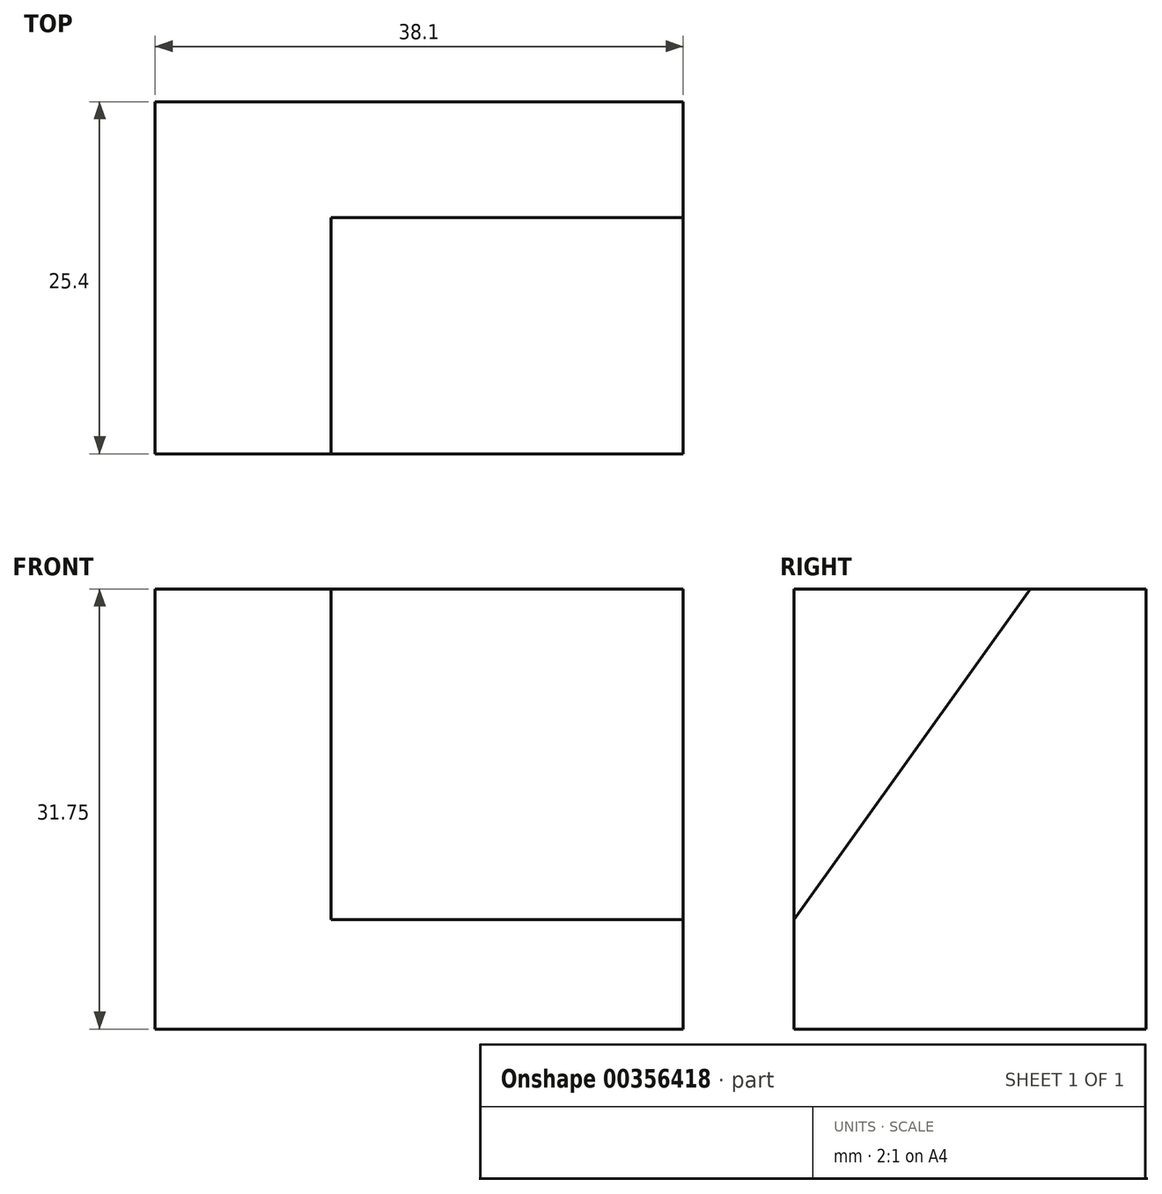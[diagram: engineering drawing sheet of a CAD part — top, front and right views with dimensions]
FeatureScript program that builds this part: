
annotation { "Feature Type Name" : "Feature", "Feature Type Description" : "" }
export const myFeature = defineFeature(function(context is Context, id is Id, definition is map)
    precondition{}
    {
        {
            var Q0;
            Q0=qCreatedBy(makeId("Front.planeOp"),FACE);
            var sketch = newSketch(context, id + "F0", { "sketchPlane" : qUnion([Q0])});
            skLineSegment(sketch, "E0", {"start": v(0, 31.75) * mm, "end": v(0, 0) * mm});
            skLineSegment(sketch, "E1", {"start": v(0, 0) * mm, "end": v(38.1, 0) * mm});
            skLineSegment(sketch, "E2", {"start": v(38.1, 0) * mm, "end": v(38.1, 31.75) * mm});
            skLineSegment(sketch, "E3", {"start": v(38.1, 31.75) * mm, "end": v(0, 31.75) * mm});
            skSolve(sketch);
        }
        {
            var Q0;
            Q0 = qSketchRegion(id + "F0", true);
            extrude(context, id + "F1", {"entities" : qUnion([Q0]), "depth" : 25.4 * mm});
        }
        {
            var Q0;
            Q0=makeQuery(id+"F1.opExtrude","SWEPT_FACE",FACE,{"disambiguationData":[OSD([sQuery(id+"F0.wireOp",EDGE,"E2")])]});
            var sketch = newSketch(context, id + "F2", { "sketchPlane" : qUnion([Q0])});
            skLineSegment(sketch, "E4", {"start": v(-8.36, 31.75) * mm, "end": v(-25.4, 7.9) * mm});
            skSolve(sketch);
        }
        {
            var Q0;
            Q0 = qSketchRegion(id + "F2", true);
            var Q1;
            {var subQ0=sQuery(id+"F2.wireOp",EDGE,"E4");Q1=makeQuery(id+"F2.imprint","IMPRINT",FACE,{"disambiguationData":[TD([[makeQuery(id+"F2.imprint","IMPRINT",EDGE,{"derivedFrom":subQ0}),-1.0]])]});}
            extrude(context, id + "F3", {"entities" : qUnion([Q0, Q1]), "operationType" : NewBodyOperationType.REMOVE, "oppositeDirection" : true, "depth" : 25.4 * mm});
        }
    });
